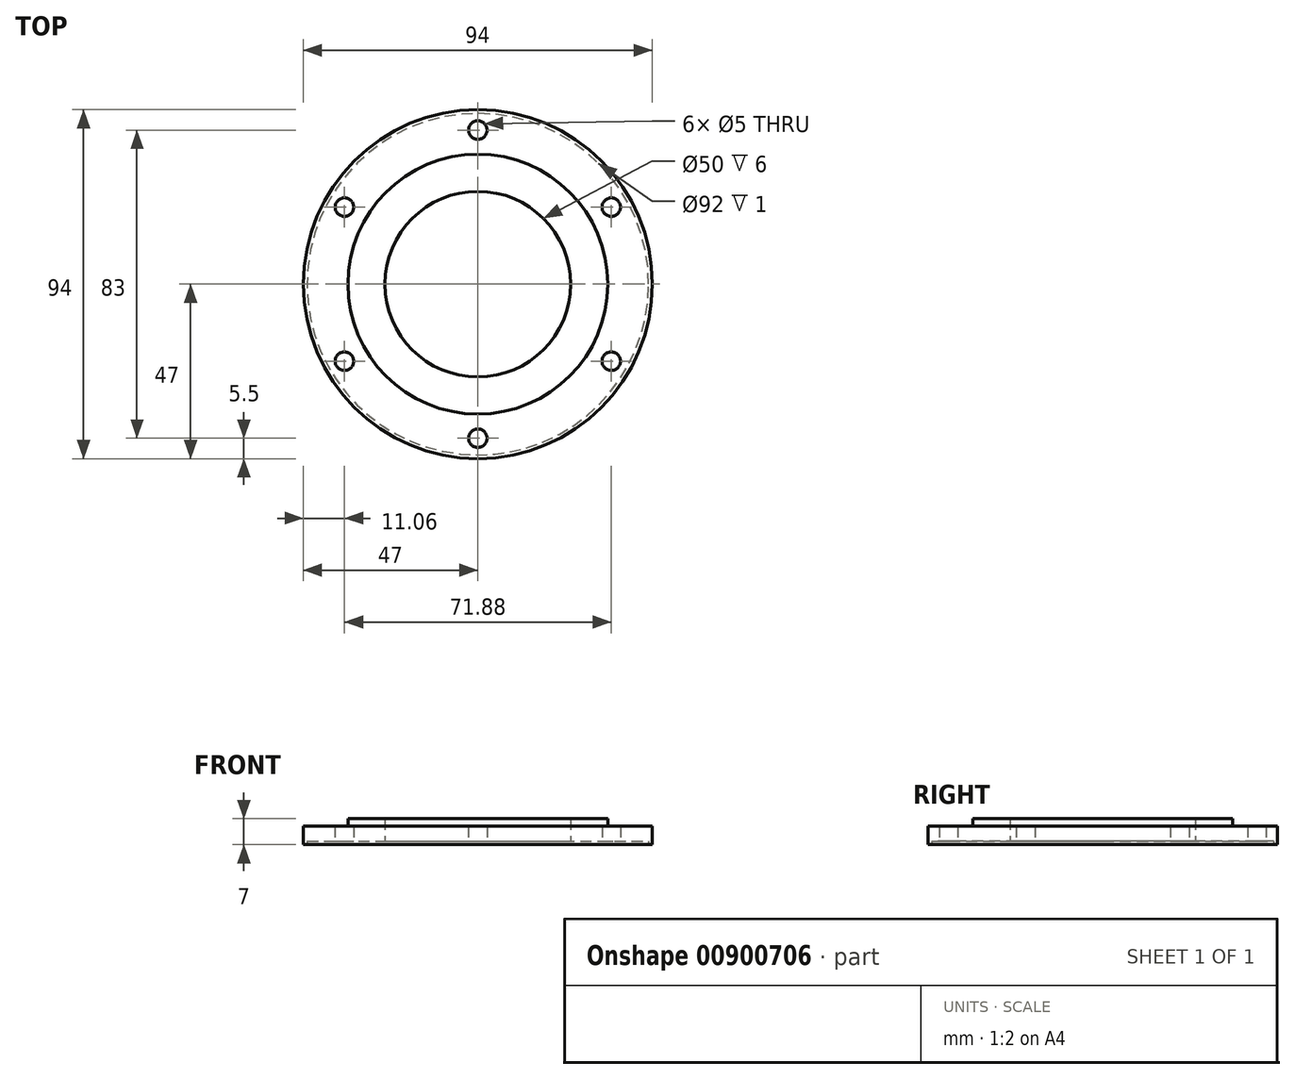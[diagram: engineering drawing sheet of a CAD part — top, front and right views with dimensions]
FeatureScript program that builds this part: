
annotation { "Feature Type Name" : "Feature", "Feature Type Description" : "" }
export const myFeature = defineFeature(function(context is Context, id is Id, definition is map)
    precondition{}
    {
        {
            var Q0;
            Q0=qCreatedBy(makeId("Top.planeOp"),FACE);
            var sketch = newSketch(context, id + "F0", { "sketchPlane" : qUnion([Q0])});
            skCircle(sketch, "E0", {"center": v(0, 0) * mm, "radius": 47 * mm});
            skCircle(sketch, "E1", {"center": v(0, 0) * mm, "radius": 25 * mm});
            skPoint(sketch, "E2", {"position": v(0, 41.5) * mm});
            skPoint(sketch, "E3", {"position": v(0, -41.5) * mm});
            skCircle(sketch, "E4", {"center": v(0, 41.5) * mm, "radius": 2.5 * mm});
            skCircle(sketch, "E5", {"center": v(0, -41.5) * mm, "radius": 2.5 * mm});
            skCircle(sketch, "E6", {"center": v(0, 0) * mm, "radius": 41.5 * mm, "construction": true});
            skPoint(sketch, "E7", {"position": v(-35.94, -20.75) * mm});
            skPoint(sketch, "E8", {"position": v(-35.94, 20.75) * mm});
            skPoint(sketch, "E9", {"position": v(35.94, 20.75) * mm});
            skPoint(sketch, "E10", {"position": v(35.94, -20.75) * mm});
            skLineSegment(sketch, "E11", {"start": v(0, 0) * mm, "end": v(35.94, -20.75) * mm, "construction": true});
            skLineSegment(sketch, "E12", {"start": v(0, 0) * mm, "end": v(35.94, 20.75) * mm, "construction": true});
            skLineSegment(sketch, "E13", {"start": v(0, 0) * mm, "end": v(-35.94, -20.75) * mm, "construction": true});
            skLineSegment(sketch, "E14", {"start": v(0, 0) * mm, "end": v(-35.94, 20.75) * mm, "construction": true});
            skCircle(sketch, "E15", {"center": v(-35.94, -20.75) * mm, "radius": 2.5 * mm});
            skCircle(sketch, "E16", {"center": v(-35.94, 20.75) * mm, "radius": 2.5 * mm});
            skCircle(sketch, "E17", {"center": v(35.94, 20.75) * mm, "radius": 2.5 * mm});
            skCircle(sketch, "E18", {"center": v(35.94, -20.75) * mm, "radius": 2.5 * mm});
            skSolve(sketch);
        }
        {
            var Q0;
            Q0 = qSketchRegion(id + "F0", true);
            extrude(context, id + "F1", {"entities" : qUnion([Q0]), "depth" : 5 * mm, "offsetDistance" : 25 * mm});
        }
        {
            var Q0;
            Q0=makeQuery(id+"F1.opExtrude","CAP_FACE",FACE,{"disambiguationData":[OSD([sQuery(id+"F0.wireOp",EDGE,"E0"),sQuery(id+"F0.wireOp",EDGE,"E1"),sQuery(id+"F0.wireOp",EDGE,"E4"),sQuery(id+"F0.wireOp",EDGE,"E5"),sQuery(id+"F0.wireOp",EDGE,"VLj2XQJf-hLgl-x4fr-N59l-gyc6k367unDZ"),sQuery(id+"F0.wireOp",EDGE,"mJwmvu8h-qoon-2emL-Uo8T-hMObTVvQVsoT"),sQuery(id+"F0.wireOp",EDGE,"Bzhvmv0A-Hyd0-RCcN-QxDl-fu7UgDC0PO29"),sQuery(id+"F0.wireOp",EDGE,"jPWbjX17-96Mn-INiJ-UpUU-O4U5pVwzj3CE"),sQuery(id+"F0.wireOp",EDGE,"6pqo1ck9-HC7M-rfRH-EZdD-FLMK1w0DReZT"),sQuery(id+"F0.wireOp",EDGE,"4z2KoF5R-CE0n-PhEb-br0U-2LOA5RvDsSWP")])],"isStart":false});
            var sketch = newSketch(context, id + "F2", { "sketchPlane" : qUnion([Q0])});
            skPoint(sketch, "E19", {"position": v(0, 0) * mm});
            skCircle(sketch, "E20", {"center": v(0, 0) * mm, "radius": 35 * mm});
            skCircle(sketch, "E21", {"center": v(0, 0) * mm, "radius": 25 * mm});
            skSolve(sketch);
        }
        {
            var Q0;
            Q0 = qSketchRegion(id + "F2", true);
            extrude(context, id + "F3", {"entities" : qUnion([Q0]), "operationType" : NewBodyOperationType.ADD, "depth" : 2 * mm, "offsetDistance" : 25 * mm});
        }
        {
            var Q0;
            Q0=makeQuery(id+"F1.opExtrude","CAP_FACE",FACE,{"disambiguationData":[OSD([sQuery(id+"F0.wireOp",EDGE,"E0"),sQuery(id+"F0.wireOp",EDGE,"E1"),sQuery(id+"F0.wireOp",EDGE,"E4"),sQuery(id+"F0.wireOp",EDGE,"E5"),sQuery(id+"F0.wireOp",EDGE,"VLj2XQJf-hLgl-x4fr-N59l-gyc6k367unDZ"),sQuery(id+"F0.wireOp",EDGE,"mJwmvu8h-qoon-2emL-Uo8T-hMObTVvQVsoT"),sQuery(id+"F0.wireOp",EDGE,"Bzhvmv0A-Hyd0-RCcN-QxDl-fu7UgDC0PO29"),sQuery(id+"F0.wireOp",EDGE,"jPWbjX17-96Mn-INiJ-UpUU-O4U5pVwzj3CE"),sQuery(id+"F0.wireOp",EDGE,"6pqo1ck9-HC7M-rfRH-EZdD-FLMK1w0DReZT"),sQuery(id+"F0.wireOp",EDGE,"4z2KoF5R-CE0n-PhEb-br0U-2LOA5RvDsSWP")])],"isStart":true});
            var sketch = newSketch(context, id + "F4", { "sketchPlane" : qUnion([Q0])});
            skCircle(sketch, "E22", {"center": v(0, 0) * mm, "radius": 46 * mm});
            skSolve(sketch);
        }
        {
            var Q0;
            Q0 = qSketchRegion(id + "F4", true);
            extrude(context, id + "F5", {"entities" : qUnion([Q0]), "operationType" : NewBodyOperationType.REMOVE, "oppositeDirection" : true, "depth" : 1 * mm, "offsetDistance" : 25 * mm});
        }
    });
